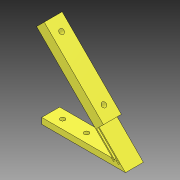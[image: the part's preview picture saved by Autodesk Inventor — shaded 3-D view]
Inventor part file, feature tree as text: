
AUTODESK INVENTOR PART (.ipt)
format: ipt  version: 2018 (Build 220112000, 112)  size: 156,160 bytes
history: native  units: mm
features: extrude x3, sketch x3, direct_edit x1, other x1
ambient origin geometry x8: Origin, YZ Plane, XZ Plane, XY Plane, X Axis, Y Axis, Z Axis, Center Point
bodies: Solid1 (feature_tree)
feature tree (8):
  direct_edit  "Direct Edit1"
  extrude  "Extrusion3"  Depth=0.3937mm
  sketch  "Sketch3"  dims[d15=4.0mm d16=4.0mm d17=7.5mm d18=0.0mm d19=50.0mm d20=10.0mm d21=10.0mm d22=0.0mm]
  sketch  "Sketch1"  dims[d1=0.0mm d2=381.0mm]
  sketch  "Sketch2"  dims[d3=101.6mm d4=0.0mm d5=508.0mm d6=101.6mm d7=190.5mm d8=254.0mm d10=0.0mm d11=381.0mm d12=0.3937mm d13=10.0mm d14=10.0mm]
  other  "Scale1"
  extrude  "Extrusion1"  Depth=4.0mm
  extrude  "Extrusion2"  Depth=10.0mm
